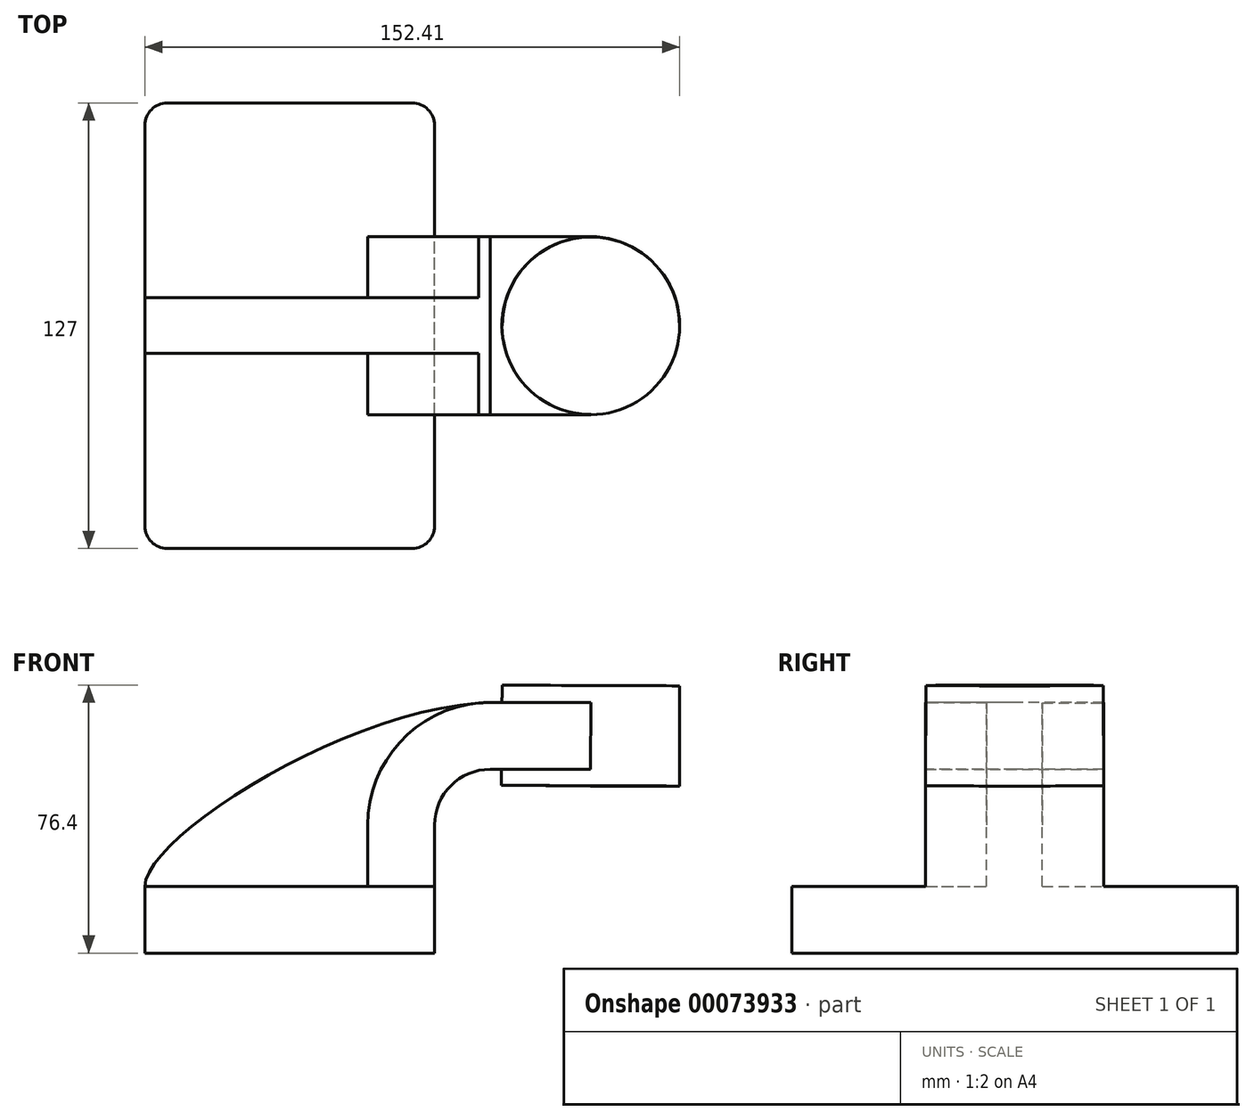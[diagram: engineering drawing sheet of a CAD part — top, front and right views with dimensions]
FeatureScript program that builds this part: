
annotation { "Feature Type Name" : "Feature", "Feature Type Description" : "" }
export const myFeature = defineFeature(function(context is Context, id is Id, definition is map)
    precondition{}
    {
        {
            var Q0;
            Q0=qCreatedBy(makeId("Front.planeOp"),FACE);
            var sketch = newSketch(context, id + "F0", { "sketchPlane" : qUnion([Q0])});
            skLineSegment(sketch, "E0.rect.bottom", {"start": v(41.28, -9.52) * mm, "end": v(-41.27, -9.52) * mm});
            skLineSegment(sketch, "E0.rect.top", {"start": v(41.27, 9.53) * mm, "end": v(-41.28, 9.53) * mm});
            skLineSegment(sketch, "E0.rect.left", {"start": v(41.28, -9.52) * mm, "end": v(41.28, 9.53) * mm});
            skLineSegment(sketch, "E0.rect.right", {"start": v(-41.27, -9.52) * mm, "end": v(-41.28, 9.53) * mm});
            skPoint(sketch, "E0.rect.middle", {"position": v(0, 0) * mm});
            skLineSegment(sketch, "E1.rect.bottom", {"start": v(60.32, 38.1) * mm, "end": v(111.12, 38.1) * mm});
            skLineSegment(sketch, "E1.rect.top", {"start": v(60.32, 66.68) * mm, "end": v(111.12, 66.68) * mm});
            skLineSegment(sketch, "E1.rect.left", {"start": v(60.32, 38.1) * mm, "end": v(60.32, 66.68) * mm});
            skLineSegment(sketch, "E1.rect.right", {"start": v(111.12, 38.1) * mm, "end": v(111.12, 66.68) * mm});
            skPoint(sketch, "E1.rect.middle", {"position": v(85.72, 52.39) * mm});
            skLineSegment(sketch, "E2", {"start": v(41.27, 9.53) * mm, "end": v(41.27, 27) * mm});
            skArc(sketch, "E3", {"start": v(41.27, 27) * mm, "mid": v(45.92, 38.23) * mm, "end": v(57.15, 42.88) * mm});
            skLineSegment(sketch, "E4", {"start": v(57.15, 42.88) * mm, "end": v(85.83, 42.88) * mm});
            skLineSegment(sketch, "E5.0", {"start": v(57.15, 61.93) * mm, "end": v(85.83, 61.93) * mm});
            skArc(sketch, "E5.1", {"start": v(22.23, 27) * mm, "mid": v(32.45, 51.7) * mm, "end": v(57.15, 61.93) * mm});
            skLineSegment(sketch, "E5.2", {"start": v(22.22, 9.53) * mm, "end": v(22.22, 27) * mm});
            skLineSegment(sketch, "E6", {"start": v(85.72, 38.1) * mm, "end": v(85.83, 66.68) * mm});
            skFitSpline(sketch, "E7", {"points": [v(-41.28, 9.53) * mm, v(57.15, 61.93) * mm], "startDerivative": vector(-0.02, 42.34) * mm, "endDerivative": vector(119.55, 2.82) * mm});
            skSolve(sketch);
        }
        {
            var Q0;
            Q0=makeQuery(id+"F0.imprint","IMPRINT",FACE,{"disambiguationData":[TD([[makeQuery(id+"F0.imprint","IMPRINT",EDGE,{"derivedFrom":sQuery(id+"F0.wireOp",EDGE,"E0.rect.bottom")}),-1.0]])]});
            extrude(context, id + "F1", {"entities" : qUnion([Q0]), "endBound" : BoundingType.SYMMETRIC, "depth" : 127 * mm});
        }
        {
            var Q0;
            {var subQ1=sQuery(id+"F0.wireOp",EDGE,"E2");Q0=makeQuery(id+"F0.imprint","IMPRINT",FACE,{"disambiguationData":[TD([[makeQuery(id+"F0.imprint","IMPRINT",EDGE,{"derivedFrom":subQ1}),1.0]])]});}
            var Q1;
            {var subQ0=sQuery(id+"F0.wireOp",EDGE,"E4");var subQ1=sQuery(id+"F0.wireOp",EDGE,"E1.rect.left");var subQ2=makeQuery(id+"F0.imprint","INTERSECT",VERTEX,{"derivedFrom":[subQ1,subQ0]});Q1=makeQuery(id+"F0.imprint","IMPRINT",FACE,{"disambiguationData":[TD([[makeQuery(id+"F0.imprint","IMPRINT",EDGE,{"disambiguationData":[TD([[subQ2,-1.0]])],"derivedFrom":subQ1}),-1.0]])]});}
            extrude(context, id + "F2", {"entities" : qUnion([Q0, Q1]), "operationType" : NewBodyOperationType.ADD, "endBound" : BoundingType.SYMMETRIC, "depth" : 50.8 * mm});
        }
        {
            var Q0;
            {var subQ3=sQuery(id+"F0.wireOp",EDGE,"E5.2");Q0=makeQuery(id+"F0.imprint","IMPRINT",FACE,{"disambiguationData":[TD([[makeQuery(id+"F0.imprint","IMPRINT",EDGE,{"derivedFrom":subQ3}),1.0]])]});}
            extrude(context, id + "F3", {"entities" : qUnion([Q0]), "operationType" : NewBodyOperationType.ADD, "endBound" : BoundingType.SYMMETRIC, "depth" : 15.88 * mm});
        }
        {
            var Q0;
            {var subQ0=sQuery(id+"F0.wireOp",EDGE,"E1.rect.right");Q0=makeQuery(id+"F0.imprint","IMPRINT",FACE,{"disambiguationData":[TD([[makeQuery(id+"F0.imprint","IMPRINT",EDGE,{"derivedFrom":subQ0}),1.0]])]});}
            var Q1;
            Q1=sQuery(id+"F0.wireOp",EDGE,"E6");
            revolve(context, id + "F4", {"operationType" : NewBodyOperationType.ADD, "entities" : qUnion([Q0]), "axis" : qUnion([Q1]), "revolveType" : RevolveType.FULL});
        }
        {
            var Q0;
            Q0=makeQuery(id+"F1.opExtrude","CAP_EDGE",EDGE,{"disambiguationData":[OSD([sQuery(id+"F0.wireOp",EDGE,"E0.rect.right")])],"isStart":false});
            var Q1;
            Q1=makeQuery(id+"F1.opExtrude","CAP_EDGE",EDGE,{"disambiguationData":[OSD([sQuery(id+"F0.wireOp",EDGE,"E0.rect.left")])],"isStart":false});
            var Q2;
            Q2=makeQuery(id+"F1.opExtrude","CAP_EDGE",EDGE,{"disambiguationData":[OSD([sQuery(id+"F0.wireOp",EDGE,"E0.rect.left")])],"isStart":true});
            var Q3;
            Q3=makeQuery(id+"F1.opExtrude","CAP_EDGE",EDGE,{"disambiguationData":[OSD([sQuery(id+"F0.wireOp",EDGE,"E0.rect.right")])],"isStart":true});
            fillet(context, id + "F5", {"entities" : qUnion([Q0, Q1, Q2, Q3]), "radius" : 6.35 * mm, "tangentPropagation" : true, "allowEdgeOverflow" : false});
        }
    });
